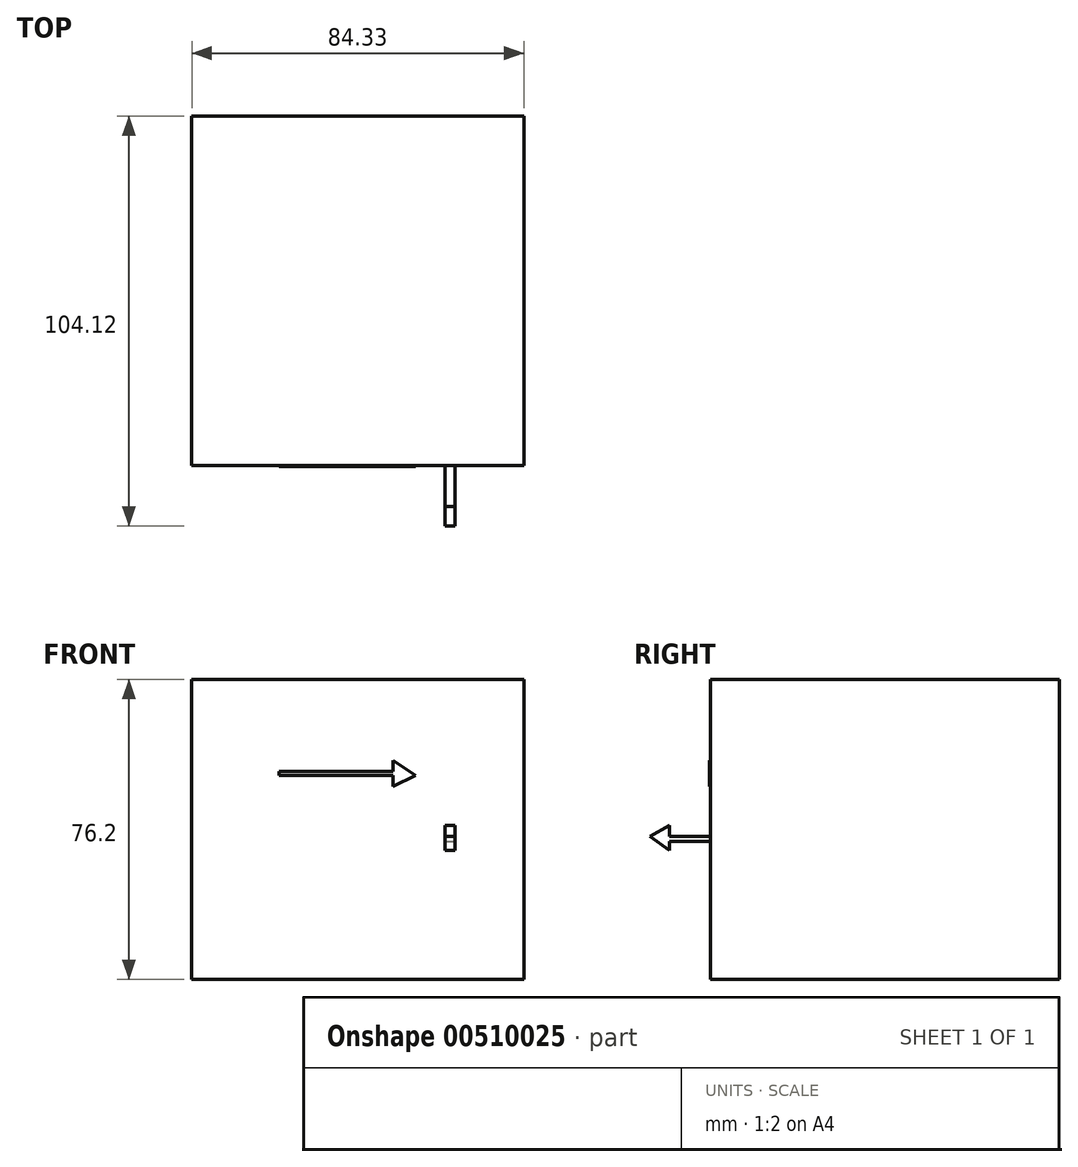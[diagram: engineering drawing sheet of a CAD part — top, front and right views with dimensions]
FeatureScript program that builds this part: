
annotation { "Feature Type Name" : "Feature", "Feature Type Description" : "" }
export const myFeature = defineFeature(function(context is Context, id is Id, definition is map)
    precondition{}
    {
        {
            var Q0;
            Q0=qCreatedBy(makeId("Top.planeOp"),FACE);
            var sketch = newSketch(context, id + "F0", { "sketchPlane" : qUnion([Q0])});
            skLineSegment(sketch, "E0.bottom", {"start": v(-38, 36.3) * mm, "end": v(46.34, 36.3) * mm});
            skLineSegment(sketch, "E0.top", {"start": v(-38, -52.45) * mm, "end": v(46.34, -52.45) * mm});
            skLineSegment(sketch, "E0.left", {"start": v(-38, 36.3) * mm, "end": v(-38, -52.45) * mm});
            skLineSegment(sketch, "E0.right", {"start": v(46.34, 36.3) * mm, "end": v(46.34, -52.45) * mm});
            skSolve(sketch);
        }
        {
            var Q0;
            Q0=makeQuery(id+"F0.imprint","IMPRINT",FACE,{"disambiguationData":[TD([[makeQuery(id+"F0.imprint","IMPRINT",EDGE,{"derivedFrom":sQuery(id+"F0.wireOp",EDGE,"E0.bottom")}),-1.0]])]});
            extrude(context, id + "F1", {"entities" : qUnion([Q0]), "depth" : 76.2 * mm});
        }
        {
            var Q0;
            Q0=makeQuery(id+"F1.opExtrude","SWEPT_FACE",FACE,{"disambiguationData":[OSD([sQuery(id+"F0.wireOp",EDGE,"E0.top")])]});
            var sketch = newSketch(context, id + "F2", { "sketchPlane" : qUnion([Q0])});
            skLineSegment(sketch, "E1", {"start": v(-38, 0) * mm, "end": v(93.02, 0) * mm});
            skLineSegment(sketch, "E2", {"start": v(93.02, 0) * mm, "end": v(93.02, 4.2) * mm});
            skLineSegment(sketch, "E3", {"start": v(93.02, 4.2) * mm, "end": v(101.13, 0) * mm});
            skLineSegment(sketch, "E4", {"start": v(-43.22, -3.08) * mm, "end": v(-27.56, -3.08) * mm});
            skSolve(sketch);
        }
        {
            var Q0;
            Q0=sQuery(id+"F2.wireOp",EDGE,"E1");
            var Q1;
            Q1=sQuery(id+"F2.wireOp",EDGE,"E4");
            revolve(context, id + "F3", {"bodyType" : ToolBodyType.SURFACE, "surfaceEntities" : qUnion([Q0]), "axis" : qUnion([Q1]), "revolveType" : RevolveType.FULL});
        }
        {
            var Q0;
            Q0=makeQuery(id+"F1.opExtrude","SWEPT_FACE",FACE,{"disambiguationData":[OSD([sQuery(id+"F0.wireOp",EDGE,"E0.top")])]});
            var sketch = newSketch(context, id + "F4", { "sketchPlane" : qUnion([Q0])});
            skLineSegment(sketch, "E5.bottom", {"start": v(-15.8, 52.86) * mm, "end": v(13.08, 52.86) * mm});
            skLineSegment(sketch, "E5.top", {"start": v(-15.8, 51.8) * mm, "end": v(13.08, 51.8) * mm});
            skLineSegment(sketch, "E5.left", {"start": v(-15.8, 52.86) * mm, "end": v(-15.8, 51.8) * mm});
            skLineSegment(sketch, "E5.right", {"start": v(13.08, 52.86) * mm, "end": v(13.08, 51.8) * mm});
            skLineSegment(sketch, "E6", {"start": v(13.08, 52.86) * mm, "end": v(13.08, 55.58) * mm});
            skLineSegment(sketch, "E7", {"start": v(13.08, 51.8) * mm, "end": v(13.08, 49.08) * mm});
            skLineSegment(sketch, "E8", {"start": v(13.08, 49.08) * mm, "end": v(18.82, 51.8) * mm});
            skLineSegment(sketch, "E9", {"start": v(18.82, 51.8) * mm, "end": v(13.08, 55.58) * mm});
            skSolve(sketch);
        }
        {
            var Q0;
            Q0=makeQuery(id+"F4.imprint","IMPRINT",FACE,{"disambiguationData":[TD([[makeQuery(id+"F4.imprint","IMPRINT",EDGE,{"derivedFrom":sQuery(id+"F4.wireOp",EDGE,"E5.bottom")}),-1.0]])]});
            var Q1;
            Q1=makeQuery(id+"F4.imprint","IMPRINT",FACE,{"disambiguationData":[TD([[makeQuery(id+"F4.imprint","IMPRINT",EDGE,{"derivedFrom":sQuery(id+"F4.wireOp",EDGE,"E5.right")}),1.0]])]});
            extrude(context, id + "F5", {"entities" : qUnion([Q0, Q1]), "operationType" : NewBodyOperationType.ADD, "depth" : 0.25 * mm});
        }
        {
            var Q0;
            Q0=makeQuery(id+"F1.opExtrude","SWEPT_FACE",FACE,{"disambiguationData":[OSD([sQuery(id+"F0.wireOp",EDGE,"E0.left")])]});
            cPlane(context, id + "F6", {"entities" : qUnion([Q0]), "cplaneType" : CPlaneType.OFFSET, "offset" : 66.8 * mm, "oppositeDirection" : true, "width" : 152.4 * mm, "height" : 152.4 * mm});
        }
        {
            var Q0;
            Q0=qCreatedBy(id+"F6.planeOp",FACE);
            var sketch = newSketch(context, id + "F7", { "sketchPlane" : qUnion([Q0])});
            skLineSegment(sketch, "E10.bottom", {"start": v(46.26, 36.38) * mm, "end": v(62.82, 36.38) * mm});
            skLineSegment(sketch, "E10.top", {"start": v(46.26, 35) * mm, "end": v(62.82, 35) * mm});
            skLineSegment(sketch, "E10.left", {"start": v(46.26, 36.38) * mm, "end": v(46.26, 35) * mm});
            skLineSegment(sketch, "E10.right", {"start": v(62.82, 36.38) * mm, "end": v(62.82, 35) * mm});
            skLineSegment(sketch, "E11", {"start": v(62.82, 35) * mm, "end": v(62.82, 32.75) * mm});
            skLineSegment(sketch, "E12", {"start": v(62.82, 32.75) * mm, "end": v(67.82, 36.38) * mm});
            skLineSegment(sketch, "E13", {"start": v(67.82, 36.38) * mm, "end": v(62.82, 39.1) * mm});
            skLineSegment(sketch, "E14", {"start": v(62.82, 39.1) * mm, "end": v(62.82, 36.38) * mm});
            skSolve(sketch);
        }
        {
            var Q0;
            Q0=makeQuery(id+"F7.imprint","IMPRINT",FACE,{"disambiguationData":[TD([[makeQuery(id+"F7.imprint","IMPRINT",EDGE,{"derivedFrom":sQuery(id+"F7.wireOp",EDGE,"E10.bottom")}),-1.0]])]});
            var Q1;
            Q1=makeQuery(id+"F7.imprint","IMPRINT",FACE,{"disambiguationData":[TD([[makeQuery(id+"F7.imprint","IMPRINT",EDGE,{"derivedFrom":sQuery(id+"F7.wireOp",EDGE,"E10.right")}),1.0]])]});
            extrude(context, id + "F8", {"entities" : qUnion([Q0, Q1]), "operationType" : NewBodyOperationType.ADD, "depth" : 2.54 * mm});
        }
    });
